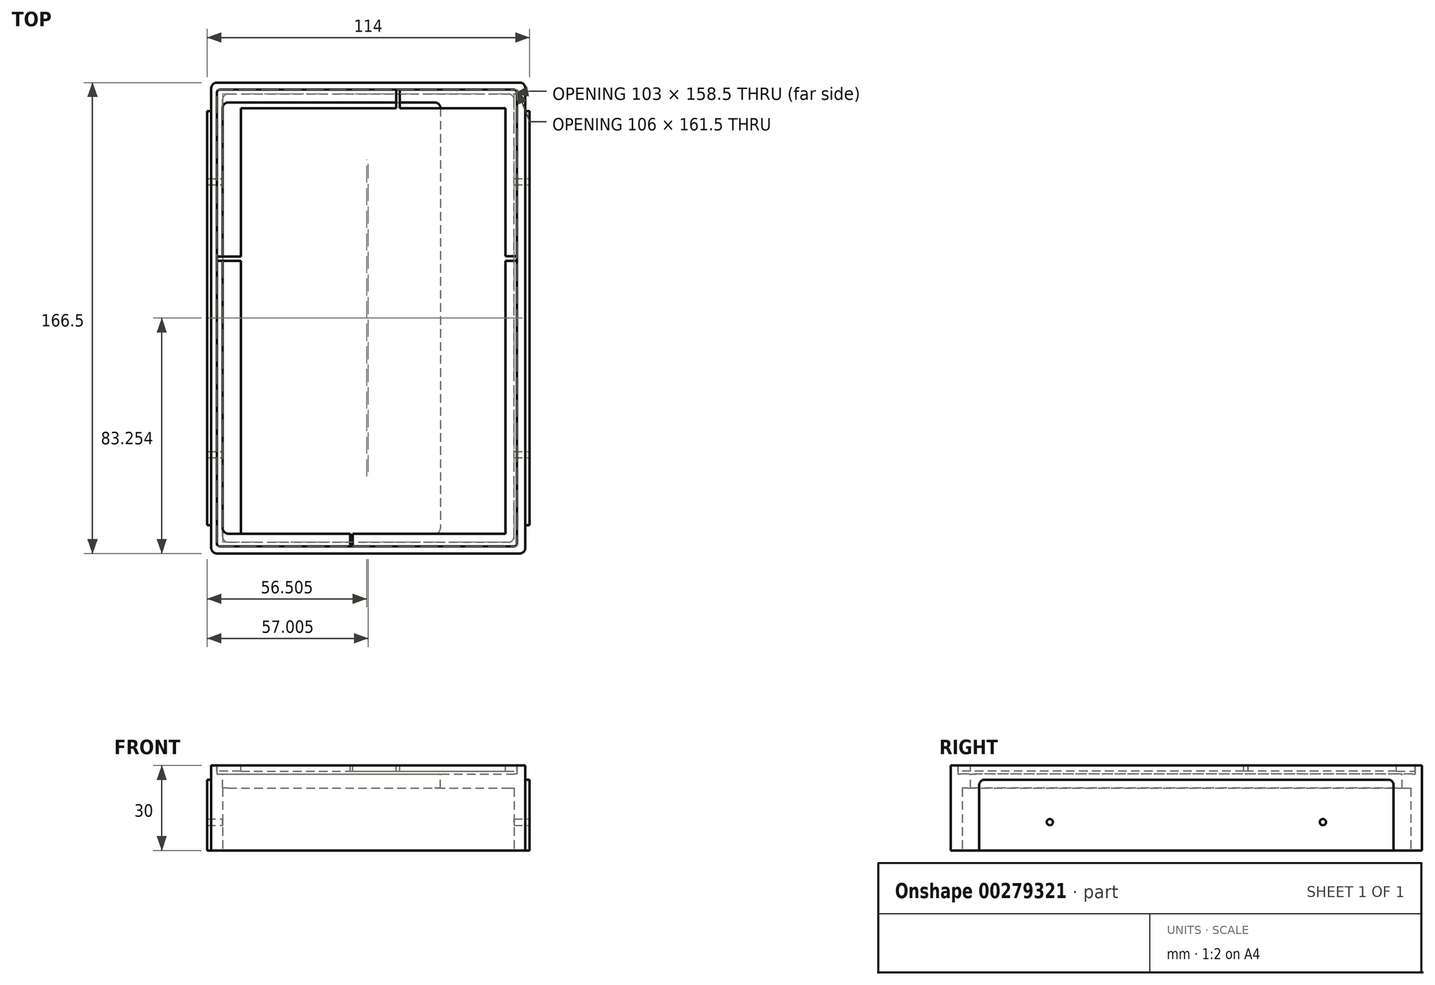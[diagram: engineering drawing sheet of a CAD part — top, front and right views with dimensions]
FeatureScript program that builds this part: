
annotation { "Feature Type Name" : "Feature", "Feature Type Description" : "" }
export const myFeature = defineFeature(function(context is Context, id is Id, definition is map)
    precondition{}
    {
        {
            var Q0;
            Q0=qCreatedBy(makeId("Top.planeOp"),FACE);
            var sketch = newSketch(context, id + "F0", { "sketchPlane" : qUnion([Q0])});
            skLineSegment(sketch, "E0.bottom", {"start": v(-57.96, 63.76) * mm, "end": v(46.04, 63.76) * mm});
            skLineSegment(sketch, "E0.top", {"start": v(-57.96, -97.74) * mm, "end": v(46.04, -97.74) * mm});
            skLineSegment(sketch, "E0.left", {"start": v(-58.96, 62.76) * mm, "end": v(-58.96, -96.74) * mm});
            skLineSegment(sketch, "E0.right", {"start": v(47.04, 62.76) * mm, "end": v(47.04, -96.74) * mm});
            skLineSegment(sketch, "E1.bottom", {"start": v(-58.96, 66.26) * mm, "end": v(48.04, 66.26) * mm});
            skLineSegment(sketch, "E1.top", {"start": v(-58.96, -100.24) * mm, "end": v(48.04, -100.24) * mm});
            skLineSegment(sketch, "E1.left", {"start": v(-60.96, 64.26) * mm, "end": v(-60.96, -98.24) * mm});
            skLineSegment(sketch, "E1.right", {"start": v(50.04, 64.26) * mm, "end": v(50.04, -98.24) * mm});
            skPoint(sketch, "E2.visualSharp", {"position": v(47.04, 63.76) * mm});
            skArc(sketch, "E2.filletArc", {"start": v(47.04, 62.76) * mm, "mid": v(46.75, 63.47) * mm, "end": v(46.04, 63.76) * mm});
            skPoint(sketch, "E3.visualSharp", {"position": v(50.04, 66.26) * mm});
            skArc(sketch, "E3.filletArc", {"start": v(50.04, 64.26) * mm, "mid": v(49.46, 65.68) * mm, "end": v(48.04, 66.26) * mm});
            skPoint(sketch, "E4.visualSharp", {"position": v(-58.96, 63.76) * mm});
            skArc(sketch, "E4.filletArc", {"start": v(-57.96, 63.76) * mm, "mid": v(-58.66, 63.47) * mm, "end": v(-58.96, 62.76) * mm});
            skPoint(sketch, "E5.visualSharp", {"position": v(-60.96, 66.26) * mm});
            skArc(sketch, "E5.filletArc", {"start": v(-58.96, 66.26) * mm, "mid": v(-60.37, 65.68) * mm, "end": v(-60.96, 64.26) * mm});
            skPoint(sketch, "E6.visualSharp", {"position": v(47.04, -97.74) * mm});
            skArc(sketch, "E6.filletArc", {"start": v(46.04, -97.74) * mm, "mid": v(46.75, -97.44) * mm, "end": v(47.04, -96.74) * mm});
            skPoint(sketch, "E7.visualSharp", {"position": v(50.04, -100.24) * mm});
            skArc(sketch, "E7.filletArc", {"start": v(48.04, -100.24) * mm, "mid": v(49.46, -99.65) * mm, "end": v(50.04, -98.24) * mm});
            skPoint(sketch, "E8.visualSharp", {"position": v(-58.96, -97.74) * mm});
            skArc(sketch, "E8.filletArc", {"start": v(-58.96, -96.74) * mm, "mid": v(-58.66, -97.44) * mm, "end": v(-57.96, -97.74) * mm});
            skPoint(sketch, "E9.visualSharp", {"position": v(-60.96, -100.24) * mm});
            skArc(sketch, "E9.filletArc", {"start": v(-60.96, -98.24) * mm, "mid": v(-60.37, -99.65) * mm, "end": v(-58.96, -100.24) * mm});
            skSolve(sketch);
        }
        {
            var Q0;
            Q0=qSketchRegion(id+"F0",true);
            extrude(context, id + "F1", {"entities" : qUnion([Q0]), "depth" : 3 * mm});
        }
        {
            var Q0;
            Q0=qCreatedBy(makeId("Top.planeOp"),FACE);
            var sketch = newSketch(context, id + "F2", { "sketchPlane" : qUnion([Q0])});
            skLineSegment(sketch, "E10.bottom", {"start": v(-58.96, 66.26) * mm, "end": v(48.04, 66.26) * mm});
            skLineSegment(sketch, "E10.top", {"start": v(-58.96, -100.24) * mm, "end": v(48.04, -100.24) * mm});
            skLineSegment(sketch, "E10.left", {"start": v(-60.96, 64.26) * mm, "end": v(-60.96, -98.24) * mm});
            skLineSegment(sketch, "E10.right", {"start": v(50.04, 64.26) * mm, "end": v(50.04, -98.24) * mm});
            skLineSegment(sketch, "E11.bottom", {"start": v(-54.96, 59.26) * mm, "end": v(18.04, 59.26) * mm});
            skLineSegment(sketch, "E11.top", {"start": v(-54.96, -93.24) * mm, "end": v(18.04, -93.24) * mm});
            skLineSegment(sketch, "E11.left", {"start": v(-56.96, 57.26) * mm, "end": v(-56.96, -91.24) * mm});
            skLineSegment(sketch, "E11.right", {"start": v(20.04, 57.26) * mm, "end": v(20.04, -91.24) * mm});
            skPoint(sketch, "E12.visualSharp", {"position": v(-56.96, -93.24) * mm});
            skArc(sketch, "E12.filletArc", {"start": v(-56.96, -91.24) * mm, "mid": v(-56.37, -92.65) * mm, "end": v(-54.96, -93.24) * mm});
            skPoint(sketch, "E13.visualSharp", {"position": v(20.04, -93.24) * mm});
            skArc(sketch, "E13.filletArc", {"start": v(18.04, -93.24) * mm, "mid": v(19.46, -92.65) * mm, "end": v(20.04, -91.24) * mm});
            skPoint(sketch, "E14.visualSharp", {"position": v(20.04, 59.26) * mm});
            skArc(sketch, "E14.filletArc", {"start": v(20.04, 57.26) * mm, "mid": v(19.46, 58.68) * mm, "end": v(18.04, 59.26) * mm});
            skPoint(sketch, "E15.visualSharp", {"position": v(-56.96, 59.26) * mm});
            skArc(sketch, "E15.filletArc", {"start": v(-54.96, 59.26) * mm, "mid": v(-56.37, 58.68) * mm, "end": v(-56.96, 57.26) * mm});
            skPoint(sketch, "E16.visualSharp", {"position": v(-60.96, -100.24) * mm});
            skArc(sketch, "E16.filletArc", {"start": v(-60.96, -98.24) * mm, "mid": v(-60.37, -99.65) * mm, "end": v(-58.96, -100.24) * mm});
            skPoint(sketch, "E17.visualSharp", {"position": v(50.04, -100.24) * mm});
            skArc(sketch, "E17.filletArc", {"start": v(48.04, -100.24) * mm, "mid": v(49.46, -99.65) * mm, "end": v(50.04, -98.24) * mm});
            skPoint(sketch, "E18.visualSharp", {"position": v(50.04, 66.26) * mm});
            skArc(sketch, "E18.filletArc", {"start": v(50.04, 64.26) * mm, "mid": v(49.46, 65.68) * mm, "end": v(48.04, 66.26) * mm});
            skPoint(sketch, "E19.visualSharp", {"position": v(-60.96, 66.26) * mm});
            skArc(sketch, "E19.filletArc", {"start": v(-58.96, 66.26) * mm, "mid": v(-60.37, 65.68) * mm, "end": v(-60.96, 64.26) * mm});
            skSolve(sketch);
        }
        {
            var Q0;
            Q0=qSketchRegion(id+"F2",true);
            extrude(context, id + "F3", {"entities" : qUnion([Q0]), "operationType" : NewBodyOperationType.ADD, "oppositeDirection" : true, "depth" : 2 * mm});
        }
        {
            var Q0;
            Q0=makeQuery(id+"F3.opExtrude","CAP_FACE",FACE,{"disambiguationData":[OSD([sQuery(id+"F2.wireOp",EDGE,"E10.bottom"),sQuery(id+"F2.wireOp",EDGE,"E10.top"),sQuery(id+"F2.wireOp",EDGE,"E10.left"),sQuery(id+"F2.wireOp",EDGE,"E10.right"),sQuery(id+"F2.wireOp",EDGE,"E11.bottom"),sQuery(id+"F2.wireOp",EDGE,"E11.top"),sQuery(id+"F2.wireOp",EDGE,"E11.left"),sQuery(id+"F2.wireOp",EDGE,"E11.right"),sQuery(id+"F2.wireOp",EDGE,"E12.filletArc"),sQuery(id+"F2.wireOp",EDGE,"E13.filletArc"),sQuery(id+"F2.wireOp",EDGE,"E14.filletArc"),sQuery(id+"F2.wireOp",EDGE,"E15.filletArc"),sQuery(id+"F2.wireOp",EDGE,"E16.filletArc"),sQuery(id+"F2.wireOp",EDGE,"E17.filletArc"),sQuery(id+"F2.wireOp",EDGE,"E18.filletArc"),sQuery(id+"F2.wireOp",EDGE,"E19.filletArc")])],"isStart":false});
            extrude(context, id + "F4", {"entities" : qUnion([Q0]), "operationType" : NewBodyOperationType.ADD, "depth" : 25 * mm});
        }
        {
            var Q0;
            Q0=makeQuery(id+"F4.opExtrude","CAP_FACE",FACE,{"disambiguationData":[OSD([sQuery(id+"F2.wireOp",EDGE,"E10.bottom"),sQuery(id+"F2.wireOp",EDGE,"E10.top"),sQuery(id+"F2.wireOp",EDGE,"E10.left"),sQuery(id+"F2.wireOp",EDGE,"E10.right"),sQuery(id+"F2.wireOp",EDGE,"E11.bottom"),sQuery(id+"F2.wireOp",EDGE,"E11.top"),sQuery(id+"F2.wireOp",EDGE,"E11.left"),sQuery(id+"F2.wireOp",EDGE,"E11.right"),sQuery(id+"F2.wireOp",EDGE,"E12.filletArc"),sQuery(id+"F2.wireOp",EDGE,"E13.filletArc"),sQuery(id+"F2.wireOp",EDGE,"E14.filletArc"),sQuery(id+"F2.wireOp",EDGE,"E15.filletArc"),sQuery(id+"F2.wireOp",EDGE,"E16.filletArc"),sQuery(id+"F2.wireOp",EDGE,"E17.filletArc"),sQuery(id+"F2.wireOp",EDGE,"E18.filletArc"),sQuery(id+"F2.wireOp",EDGE,"E19.filletArc")])],"isStart":false});
            var sketch = newSketch(context, id + "F5", { "sketchPlane" : qUnion([Q0])});
            skLineSegment(sketch, "E20.bottom", {"start": v(-54.96, 96.24) * mm, "end": v(44.04, 96.24) * mm});
            skLineSegment(sketch, "E20.top", {"start": v(-54.96, -62.26) * mm, "end": v(44.04, -62.26) * mm});
            skLineSegment(sketch, "E20.left", {"start": v(-56.96, 94.24) * mm, "end": v(-56.96, -60.26) * mm});
            skLineSegment(sketch, "E20.right", {"start": v(46.04, 94.24) * mm, "end": v(46.04, -60.26) * mm});
            skPoint(sketch, "E21.visualSharp", {"position": v(-56.96, 93.24) * mm});
            skArc(sketch, "E21.filletArc", {"start": v(-54.96, 96.24) * mm, "mid": v(-56.37, 95.65) * mm, "end": v(-56.96, 94.24) * mm});
            skPoint(sketch, "E22.visualSharp", {"position": v(46.04, 96.24) * mm});
            skArc(sketch, "E22.filletArc", {"start": v(46.04, 94.24) * mm, "mid": v(45.46, 95.65) * mm, "end": v(44.04, 96.24) * mm});
            skPoint(sketch, "E23.visualSharp", {"position": v(46.04, -62.26) * mm});
            skArc(sketch, "E23.filletArc", {"start": v(44.04, -62.26) * mm, "mid": v(45.46, -61.68) * mm, "end": v(46.04, -60.26) * mm});
            skPoint(sketch, "E24.visualSharp", {"position": v(-56.96, -62.26) * mm});
            skArc(sketch, "E24.filletArc", {"start": v(-56.96, -60.26) * mm, "mid": v(-56.37, -61.68) * mm, "end": v(-54.96, -62.26) * mm});
            skSolve(sketch);
        }
        {
            var Q0;
            Q0=qSketchRegion(id+"F5",true);
            extrude(context, id + "F6", {"entities" : qUnion([Q0]), "operationType" : NewBodyOperationType.REMOVE, "oppositeDirection" : true, "depth" : 22 * mm});
        }
        {
            var Q0;
            Q0=makeQuery(id+"F1.opExtrude","CAP_FACE",FACE,{"disambiguationData":[OSD([sQuery(id+"F0.wireOp",EDGE,"E0.bottom"),sQuery(id+"F0.wireOp",EDGE,"E0.top"),sQuery(id+"F0.wireOp",EDGE,"E0.left"),sQuery(id+"F0.wireOp",EDGE,"E0.right"),sQuery(id+"F0.wireOp",EDGE,"E1.bottom"),sQuery(id+"F0.wireOp",EDGE,"E1.top"),sQuery(id+"F0.wireOp",EDGE,"E1.left"),sQuery(id+"F0.wireOp",EDGE,"E1.right"),sQuery(id+"F0.wireOp",EDGE,"E2.filletArc"),sQuery(id+"F0.wireOp",EDGE,"E3.filletArc"),sQuery(id+"F0.wireOp",EDGE,"E4.filletArc"),sQuery(id+"F0.wireOp",EDGE,"E5.filletArc"),sQuery(id+"F0.wireOp",EDGE,"E6.filletArc"),sQuery(id+"F0.wireOp",EDGE,"E7.filletArc"),sQuery(id+"F0.wireOp",EDGE,"E8.filletArc"),sQuery(id+"F0.wireOp",EDGE,"E9.filletArc")])],"isStart":false});
            var sketch = newSketch(context, id + "F7", { "sketchPlane" : qUnion([Q0])});
            skLineSegment(sketch, "E25.bottom", {"start": v(-50.46, 57.26) * mm, "end": v(43.04, 57.26) * mm});
            skLineSegment(sketch, "E25.top", {"start": v(-50.46, -93.24) * mm, "end": v(43.04, -93.24) * mm});
            skLineSegment(sketch, "E25.left", {"start": v(-50.46, 57.26) * mm, "end": v(-50.46, -93.24) * mm});
            skLineSegment(sketch, "E25.right", {"start": v(43.04, 57.26) * mm, "end": v(43.04, -93.24) * mm});
            skLineSegment(sketch, "E26.bottom", {"start": v(4.39, 57.26) * mm, "end": v(5.73, 57.26) * mm});
            skLineSegment(sketch, "E26.top", {"start": v(4.39, 63.76) * mm, "end": v(5.73, 63.76) * mm});
            skLineSegment(sketch, "E26.left", {"start": v(4.39, 57.26) * mm, "end": v(4.39, 63.76) * mm});
            skLineSegment(sketch, "E26.right", {"start": v(5.73, 57.26) * mm, "end": v(5.73, 63.76) * mm});
            skLineSegment(sketch, "E27.bottom", {"start": v(-50.46, 4.74) * mm, "end": v(-58.96, 4.74) * mm});
            skLineSegment(sketch, "E27.top", {"start": v(-50.46, 3.27) * mm, "end": v(-58.96, 3.27) * mm});
            skLineSegment(sketch, "E27.left", {"start": v(-50.46, 4.74) * mm, "end": v(-50.46, 3.27) * mm});
            skLineSegment(sketch, "E27.right", {"start": v(-58.96, 4.74) * mm, "end": v(-58.96, 3.27) * mm});
            skLineSegment(sketch, "E28.bottom", {"start": v(-11.88, -93.24) * mm, "end": v(-11.02, -93.24) * mm});
            skLineSegment(sketch, "E28.top", {"start": v(-11.88, -97.74) * mm, "end": v(-11.02, -97.74) * mm});
            skLineSegment(sketch, "E28.left", {"start": v(-11.88, -93.24) * mm, "end": v(-11.88, -97.74) * mm});
            skLineSegment(sketch, "E28.right", {"start": v(-11.02, -93.24) * mm, "end": v(-11.02, -97.74) * mm});
            skLineSegment(sketch, "E29.bottom", {"start": v(43.04, 4.9) * mm, "end": v(47.04, 4.9) * mm});
            skLineSegment(sketch, "E29.top", {"start": v(43.04, 3.27) * mm, "end": v(47.04, 3.27) * mm});
            skLineSegment(sketch, "E29.left", {"start": v(43.04, 4.9) * mm, "end": v(43.04, 3.27) * mm});
            skLineSegment(sketch, "E29.right", {"start": v(47.04, 4.9) * mm, "end": v(47.04, 3.27) * mm});
            skSolve(sketch);
        }
        {
            var Q0;
            Q0=qSketchRegion(id+"F7",true);
            extrude(context, id + "F8", {"entities" : qUnion([Q0]), "oppositeDirection" : true, "depth" : 2 * mm});
        }
        {
            var Q0;
            {var subQ0=sQuery(id+"F2.wireOp",EDGE,"E10.left");Q0=makeQuery(id+"F4.boolean.opBoolean","MERGE",FACE,{"derivedFrom":[makeQuery(id+"F3.boolean.opBoolean","MERGE",FACE,{"derivedFrom":[makeQuery(id+"F1.opExtrude","SWEPT_FACE",FACE,{"disambiguationData":[OSD([sQuery(id+"F0.wireOp",EDGE,"E1.left")])]}),makeQuery(id+"F3.opExtrude","SWEPT_FACE",FACE,{"disambiguationData":[OSD([subQ0])]})]}),makeQuery(id+"F4.opExtrude","SWEPT_FACE",FACE,{"disambiguationData":[OSD([subQ0])]})]});}
            var sketch = newSketch(context, id + "F9", { "sketchPlane" : qUnion([Q0])});
            skLineSegment(sketch, "E30.bottom", {"start": v(-54.26, -2) * mm, "end": v(88.24, -2) * mm});
            skLineSegment(sketch, "E30.top", {"start": v(-56.26, -27) * mm, "end": v(90.24, -27) * mm});
            skLineSegment(sketch, "E30.left", {"start": v(-56.26, -4) * mm, "end": v(-56.26, -27) * mm});
            skLineSegment(sketch, "E30.right", {"start": v(90.24, -4) * mm, "end": v(90.24, -27) * mm});
            skPoint(sketch, "E31.visualSharp", {"position": v(-56.26, -2) * mm});
            skArc(sketch, "E31.filletArc", {"start": v(-54.26, -2) * mm, "mid": v(-55.68, -2.59) * mm, "end": v(-56.26, -4) * mm});
            skPoint(sketch, "E32.visualSharp", {"position": v(90.24, -2) * mm});
            skArc(sketch, "E32.filletArc", {"start": v(90.24, -4) * mm, "mid": v(89.65, -2.59) * mm, "end": v(88.24, -2) * mm});
            skSolve(sketch);
        }
        {
            var Q0;
            Q0=qSketchRegion(id+"F9",true);
            extrude(context, id + "F10", {"entities" : qUnion([Q0]), "operationType" : NewBodyOperationType.ADD, "depth" : 1.5 * mm});
        }
        {
            var Q0;
            {var subQ0=sQuery(id+"F2.wireOp",EDGE,"E10.right");Q0=makeQuery(id+"F4.boolean.opBoolean","MERGE",FACE,{"derivedFrom":[makeQuery(id+"F3.boolean.opBoolean","MERGE",FACE,{"derivedFrom":[makeQuery(id+"F1.opExtrude","SWEPT_FACE",FACE,{"disambiguationData":[OSD([sQuery(id+"F0.wireOp",EDGE,"E1.right")])]}),makeQuery(id+"F3.opExtrude","SWEPT_FACE",FACE,{"disambiguationData":[OSD([subQ0])]})]}),makeQuery(id+"F4.opExtrude","SWEPT_FACE",FACE,{"disambiguationData":[OSD([subQ0])]})]});}
            var sketch = newSketch(context, id + "F11", { "sketchPlane" : qUnion([Q0])});
            skLineSegment(sketch, "E33.bottom", {"start": v(-88.24, -2) * mm, "end": v(54.26, -2) * mm});
            skLineSegment(sketch, "E33.top", {"start": v(-90.24, -27) * mm, "end": v(56.26, -27) * mm});
            skLineSegment(sketch, "E33.left", {"start": v(-90.24, -4) * mm, "end": v(-90.24, -27) * mm});
            skLineSegment(sketch, "E33.right", {"start": v(56.26, -4) * mm, "end": v(56.26, -27) * mm});
            skPoint(sketch, "E34.visualSharp", {"position": v(-90.24, -2) * mm});
            skArc(sketch, "E34.filletArc", {"start": v(-88.24, -2) * mm, "mid": v(-89.65, -2.59) * mm, "end": v(-90.24, -4) * mm});
            skPoint(sketch, "E35.visualSharp", {"position": v(56.26, -2) * mm});
            skArc(sketch, "E35.filletArc", {"start": v(56.26, -4) * mm, "mid": v(55.68, -2.59) * mm, "end": v(54.26, -2) * mm});
            skSolve(sketch);
        }
        {
            var Q0;
            Q0=qSketchRegion(id+"F11",true);
            extrude(context, id + "F12", {"entities" : qUnion([Q0]), "operationType" : NewBodyOperationType.ADD, "depth" : 1.5 * mm});
        }
        {
            var Q0;
            Q0=makeQuery(id+"F12.opExtrude","CAP_FACE",FACE,{"disambiguationData":[OSD([sQuery(id+"F11.wireOp",EDGE,"E33.bottom"),sQuery(id+"F11.wireOp",EDGE,"E33.top"),sQuery(id+"F11.wireOp",EDGE,"E33.left"),sQuery(id+"F11.wireOp",EDGE,"E33.right"),sQuery(id+"F11.wireOp",EDGE,"E34.filletArc"),sQuery(id+"F11.wireOp",EDGE,"E35.filletArc")])],"isStart":false});
            var sketch = newSketch(context, id + "F13", { "sketchPlane" : qUnion([Q0])});
            skCircle(sketch, "E36", {"center": v(-65.24, -17) * mm, "radius": 1.1 * mm});
            skCircle(sketch, "E37", {"center": v(31.26, -17) * mm, "radius": 1.1 * mm});
            skSolve(sketch);
        }
        {
            var Q0;
            Q0=qSketchRegion(id+"F13",true);
            extrude(context, id + "F14", {"entities" : qUnion([Q0]), "operationType" : NewBodyOperationType.REMOVE, "oppositeDirection" : true, "depth" : 120 * mm});
        }
        {
            var Q0;
            Q0=makeQuery(id+"F1.opExtrude","SWEPT_BODY",BODY,{"disambiguationData":[OSD([sQuery(id+"F0.wireOp",EDGE,"E0.bottom"),sQuery(id+"F0.wireOp",EDGE,"E0.top"),sQuery(id+"F0.wireOp",EDGE,"E0.left"),sQuery(id+"F0.wireOp",EDGE,"E0.right"),sQuery(id+"F0.wireOp",EDGE,"E1.bottom"),sQuery(id+"F0.wireOp",EDGE,"E1.top"),sQuery(id+"F0.wireOp",EDGE,"E1.left"),sQuery(id+"F0.wireOp",EDGE,"E1.right"),sQuery(id+"F0.wireOp",EDGE,"E2.filletArc"),sQuery(id+"F0.wireOp",EDGE,"E3.filletArc"),sQuery(id+"F0.wireOp",EDGE,"E4.filletArc"),sQuery(id+"F0.wireOp",EDGE,"E5.filletArc"),sQuery(id+"F0.wireOp",EDGE,"E6.filletArc"),sQuery(id+"F0.wireOp",EDGE,"E7.filletArc"),sQuery(id+"F0.wireOp",EDGE,"E8.filletArc"),sQuery(id+"F0.wireOp",EDGE,"E9.filletArc")])]});
            transform(context, id + "F15", {"entities" : qUnion([Q0]), "transformType" : TransformType.TRANSLATION_3D, "dx" : 0 * mm, "dy" : 0 * mm, "dz" : 0 * mm, "makeCopy" : true});
        }
    });
